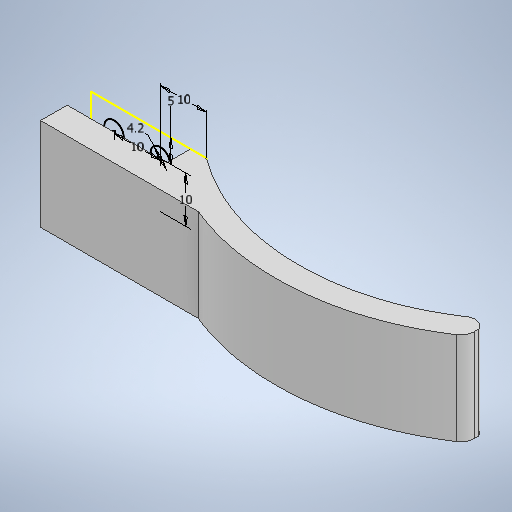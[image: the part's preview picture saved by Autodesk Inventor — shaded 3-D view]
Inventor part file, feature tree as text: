
AUTODESK INVENTOR PART (.ipt)
format: ipt  version: 2025.1 (Build 291241000, 241)  size: 265,216 bytes
history: native  units: mm
features: sketch x3, extrude x2, fillet x2, projected_geometry x1
ambient origin geometry x8: Origin, YZ Plane, XZ Plane, XY Plane, X Axis, Y Axis, Z Axis, Center Point
bodies: Solid1 (feature_tree)
feature tree (8):
  extrude  "Extrusion1"  Depth=100.0mm
  extrude  "Extrusion2"  Depth=20.0mm TaperAngle=0.0deg
  fillet  "Fillet1"  Radius=4.2mm
  fillet  "Fillet2"  Radius=10.0mm
  sketch  "Sketch1"  dims[d0=60.0mm d2=100.0mm]
  sketch  "Sketch2"  dims[d9=20.0mm d11=10.0mm d12=20.0mm d14=10.0mm d17=10.0mm d18=5.0mm d19=20.0mm d20=0.0mm d21=3.0mm d22=2.5mm d23=1.428888mm]
  projected_geometry  "Projected Loop1"
  sketch  "Sketch Rectangular Pattern1"  dims[d5=4.999995mm d6=20.0mm d7=0.0mm d8=4.2mm]
